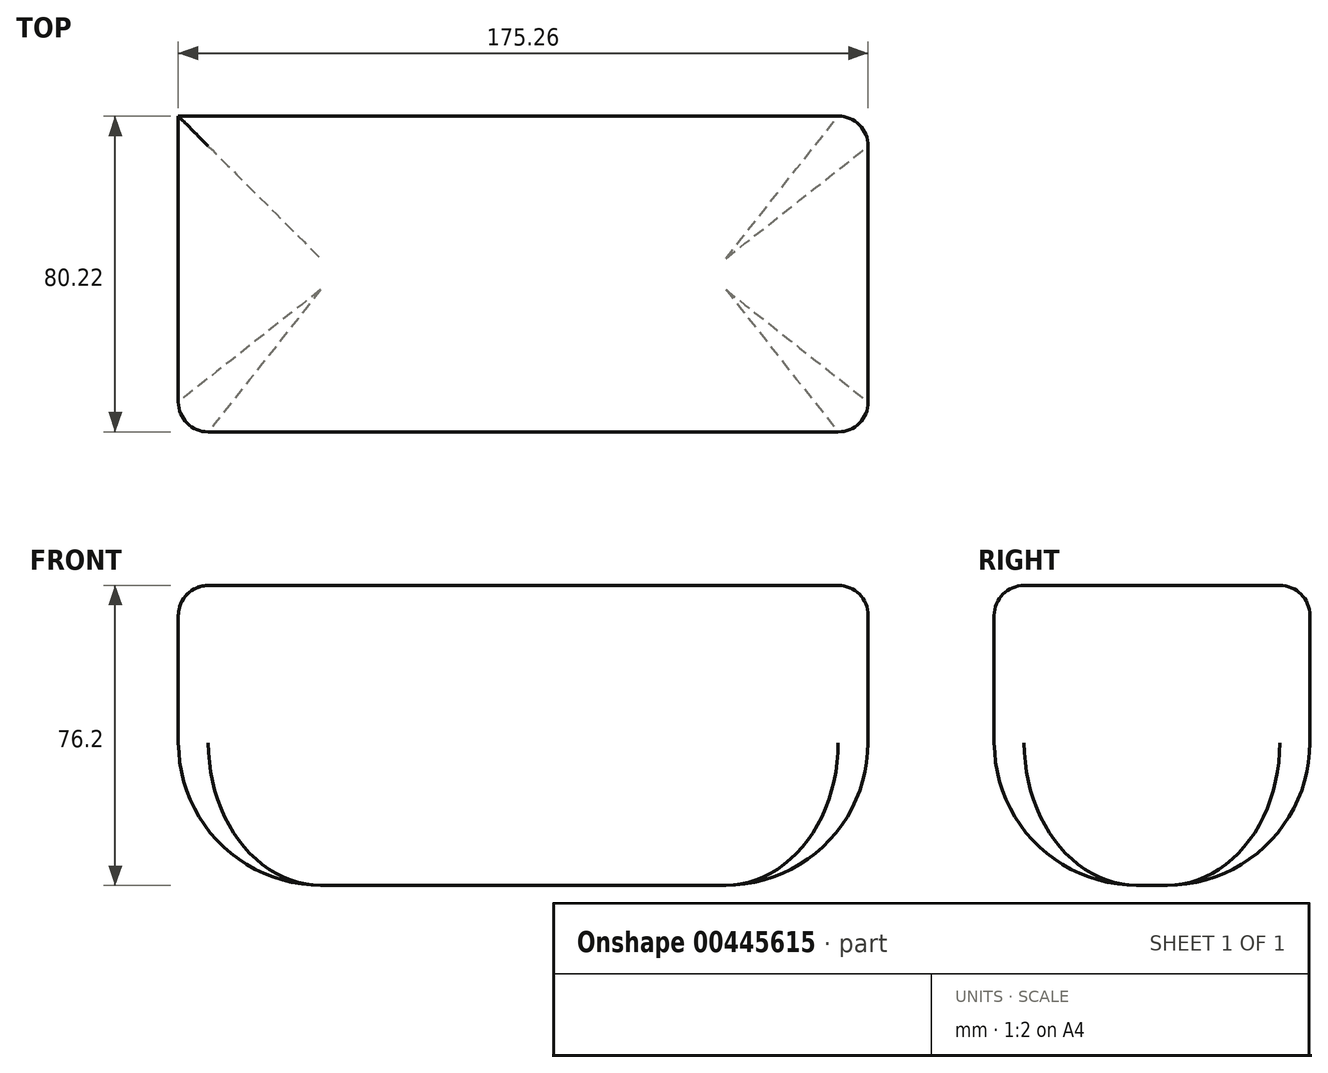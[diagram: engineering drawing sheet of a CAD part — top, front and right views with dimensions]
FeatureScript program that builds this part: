
annotation { "Feature Type Name" : "Feature", "Feature Type Description" : "" }
export const myFeature = defineFeature(function(context is Context, id is Id, definition is map)
    precondition{}
    {
        {
            var Q0;
            Q0=qCreatedBy(makeId("Top.planeOp"),FACE);
            var sketch = newSketch(context, id + "F0", { "sketchPlane" : qUnion([Q0])});
            skLineSegment(sketch, "E0.bottom", {"start": v(87.63, -40.1) * mm, "end": v(-87.63, -40.1) * mm});
            skLineSegment(sketch, "E0.top", {"start": v(87.63, 40.1) * mm, "end": v(-87.63, 40.1) * mm});
            skLineSegment(sketch, "E0.left", {"start": v(87.63, -40.1) * mm, "end": v(87.63, 40.1) * mm});
            skLineSegment(sketch, "E0.right", {"start": v(-87.63, -40.1) * mm, "end": v(-87.63, 40.1) * mm});
            skPoint(sketch, "E0.middle", {"position": v(0, 0) * mm});
            skLineSegment(sketch, "E1.bottom", {"start": v(87.63, -40.1) * mm, "end": v(87.63, -40.1) * mm});
            skLineSegment(sketch, "E1.left", {"start": v(87.63, -40.1) * mm, "end": v(87.63, -40.1) * mm});
            skLineSegment(sketch, "E1.right", {"start": v(87.63, -40.1) * mm, "end": v(87.63, -40.1) * mm});
            skPoint(sketch, "E1.middle", {"position": v(87.63, -40.1) * mm});
            skSolve(sketch);
        }
        {
            var Q0;
            Q0 = qSketchRegion(id + "F0", true);
            extrude(context, id + "F1", {"entities" : qUnion([Q0]), "depth" : 76.2 * mm});
        }
        {
            var Q0;
            Q0=makeQuery(id+"F1.opExtrude","CAP_EDGE",EDGE,{"disambiguationData":[OSD([sQuery(id+"F0.wireOp",EDGE,"E0.bottom")])],"isStart":false});
            fillet(context, id + "F2", {"entities" : qUnion([Q0]), "radius" : 7.62 * mm, "tangentPropagation" : true, "allowEdgeOverflow" : false});
        }
        {
            var Q0;
            Q0=makeQuery(id+"F1.opExtrude","CAP_EDGE",EDGE,{"disambiguationData":[OSD([sQuery(id+"F0.wireOp",EDGE,"E0.left")])],"isStart":false});
            fillet(context, id + "F3", {"entities" : qUnion([Q0]), "radius" : 7.62 * mm, "tangentPropagation" : true, "allowEdgeOverflow" : false});
        }
        {
            var Q0;
            Q0=makeQuery(id+"F1.opExtrude","CAP_EDGE",EDGE,{"disambiguationData":[OSD([sQuery(id+"F0.wireOp",EDGE,"E0.top")])],"isStart":false});
            var Q1;
            Q1=makeQuery(id+"F1.opExtrude","SWEPT_EDGE",EDGE,{"disambiguationData":[OSD([sQuery(id+"F0.wireOp",EDGE,"E0.bottom"),sQuery(id+"F0.wireOp",EDGE,"E0.right")])]});
            fillet(context, id + "F4", {"entities" : qUnion([Q0, Q1]), "radius" : 7.62 * mm, "tangentPropagation" : true, "allowEdgeOverflow" : false});
        }
        {
            var Q0;
            Q0=makeQuery(id+"F1.opExtrude","CAP_EDGE",EDGE,{"disambiguationData":[OSD([sQuery(id+"F0.wireOp",EDGE,"E0.bottom")])],"isStart":true});
            var Q1;
            Q1=makeQuery(id+"F1.opExtrude","CAP_EDGE",EDGE,{"disambiguationData":[OSD([sQuery(id+"F0.wireOp",EDGE,"E0.left")])],"isStart":true});
            fillet(context, id + "F5", {"entities" : qUnion([Q0, Q1]), "radius" : 36.18 * mm, "tangentPropagation" : true, "allowEdgeOverflow" : false});
        }
    });
